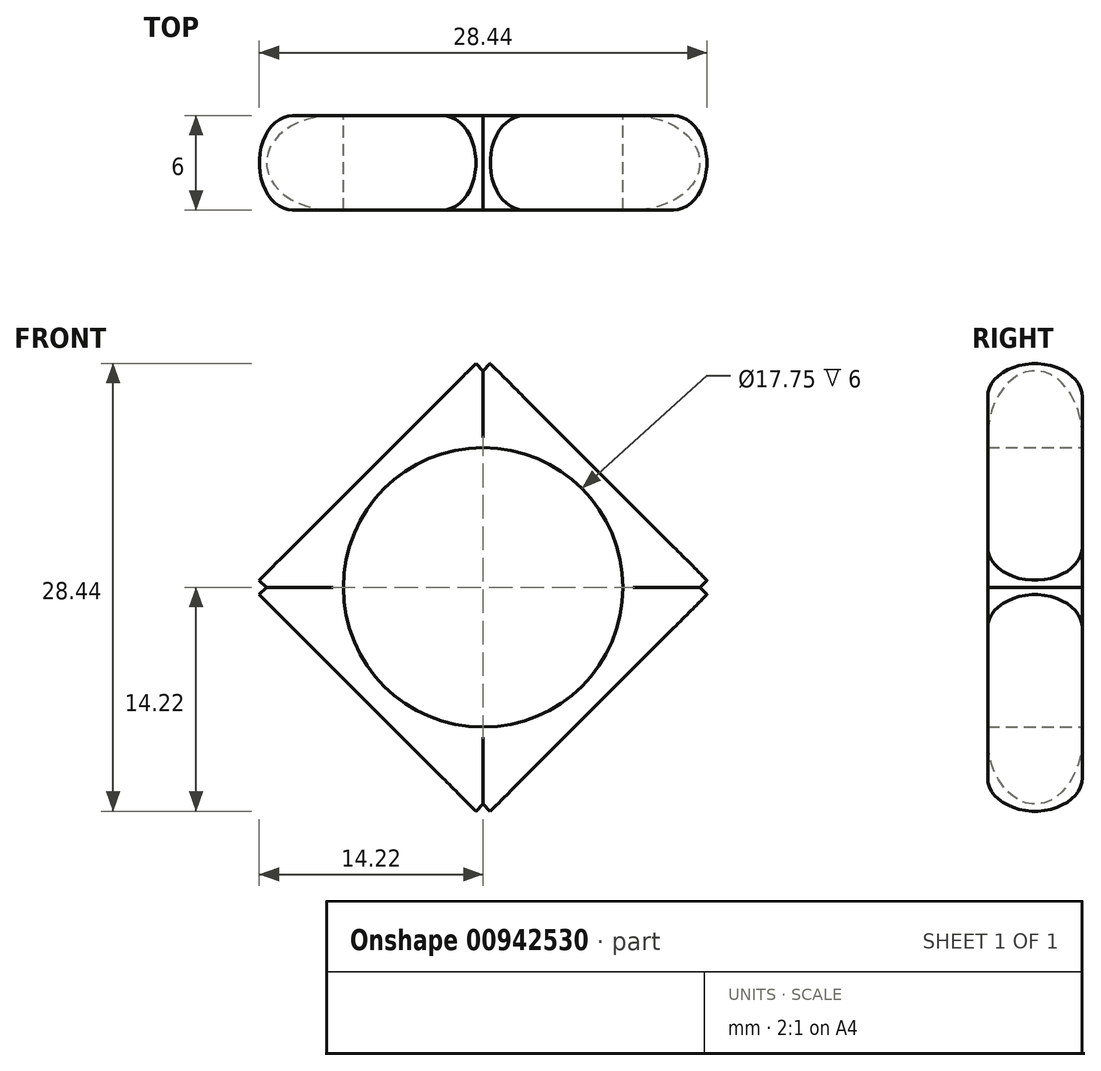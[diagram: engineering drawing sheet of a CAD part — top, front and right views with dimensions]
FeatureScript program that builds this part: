
annotation { "Feature Type Name" : "Feature", "Feature Type Description" : "" }
export const myFeature = defineFeature(function(context is Context, id is Id, definition is map)
    precondition{}
    {
        {
            var Q0;
            Q0=qCreatedBy(makeId("Front.planeOp"),FACE);
            var sketch = newSketch(context, id + "F0", { "sketchPlane" : qUnion([Q0])});
            skCircle(sketch, "E0", {"center": v(0, 0) * mm, "radius": 8.88 * mm});
            skCircle(sketch, "E1.0", {"center": v(0, 0) * mm, "radius": 10.38 * mm});
            skLineSegment(sketch, "E2", {"start": v(0, 10.37) * mm, "end": v(0, 11.88) * mm, "construction": true});
            skLineSegment(sketch, "E3", {"start": v(-14.67, 0) * mm, "end": v(0, 14.67) * mm});
            skLineSegment(sketch, "E4.MirrorCS", {"start": v(14.67, 0) * mm, "end": v(0, 14.67) * mm});
            skLineSegment(sketch, "E5.MirrorCS", {"start": v(14.67, 0) * mm, "end": v(0, -14.67) * mm});
            skLineSegment(sketch, "E6.MirrorCS", {"start": v(-14.67, 0) * mm, "end": v(0, -14.67) * mm});
            skLineSegment(sketch, "E7", {"start": v(-0.46, 14.22) * mm, "end": v(0, 13.76) * mm});
            skLineSegment(sketch, "E8", {"start": v(0, 13.76) * mm, "end": v(0.46, 14.22) * mm});
            skLineSegment(sketch, "E9.MirrorCS", {"start": v(0, -13.76) * mm, "end": v(0.46, -14.22) * mm});
            skLineSegment(sketch, "E10.MirrorCS", {"start": v(-0.46, -14.22) * mm, "end": v(0, -13.76) * mm});
            skLineSegment(sketch, "E11", {"start": v(14.22, 0.46) * mm, "end": v(13.76, 0) * mm});
            skLineSegment(sketch, "E12", {"start": v(13.76, 0) * mm, "end": v(14.22, -0.46) * mm});
            skLineSegment(sketch, "E13.MirrorCS", {"start": v(-14.22, 0.46) * mm, "end": v(-13.76, 0) * mm});
            skLineSegment(sketch, "E14.MirrorCS", {"start": v(-13.76, 0) * mm, "end": v(-14.22, -0.46) * mm});
            skPoint(sketch, "E15.orphan", {"position": v(-10.37, 0) * mm});
            skSolve(sketch);
        }
        {
            var Q0;
            {var subQ0=sQuery(id+"F0.wireOp",EDGE,"E7");Q0=makeQuery(id+"F0.imprint","IMPRINT",FACE,{"disambiguationData":[TD([[makeQuery(id+"F0.imprint","IMPRINT",EDGE,{"derivedFrom":subQ0}),-1.0]])]});}
            var Q1;
            {var subQ0=sQuery(id+"F0.wireOp",EDGE,"E13.MirrorCS");Q1=makeQuery(id+"F0.imprint","IMPRINT",FACE,{"disambiguationData":[TD([[makeQuery(id+"F0.imprint","IMPRINT",EDGE,{"derivedFrom":subQ0}),1.0]])]});}
            var Q2;
            Q2=makeQuery(id+"F0.imprint","IMPRINT",FACE,{"disambiguationData":[TD([[makeQuery(id+"F0.imprint","IMPRINT",EDGE,{"derivedFrom":sQuery(id+"F0.wireOp",EDGE,"E0")}),-1.0]])]});
            var Q3;
            {var subQ7=sQuery(id+"F0.wireOp",EDGE,"E11");Q3=makeQuery(id+"F0.imprint","IMPRINT",FACE,{"disambiguationData":[TD([[makeQuery(id+"F0.imprint","IMPRINT",EDGE,{"derivedFrom":subQ7}),-1.0]])]});}
            var Q4;
            {var subQ0=sQuery(id+"F0.wireOp",EDGE,"E9.MirrorCS");Q4=makeQuery(id+"F0.imprint","IMPRINT",FACE,{"disambiguationData":[TD([[makeQuery(id+"F0.imprint","IMPRINT",EDGE,{"derivedFrom":subQ0}),1.0]])]});}
            extrude(context, id + "F1", {"entities" : qUnion([Q0, Q1, Q2, Q3, Q4]), "depth" : 3 * mm, "offsetDistance" : 25 * mm, "hasSecondDirection" : true, "secondDirectionOppositeDirection" : true, "secondDirectionDepth" : 3 * mm});
        }
        {
            var Q0;
            Q0=makeQuery(id+"F1.opExtrude","CAP_EDGE",EDGE,{"disambiguationData":[OSD([sQuery(id+"F0.wireOp",EDGE,"E8")])],"isStart":false});
            var Q1;
            Q1=makeQuery(id+"F1.opExtrude","CAP_EDGE",EDGE,{"disambiguationData":[OSD([sQuery(id+"F0.wireOp",EDGE,"E7")])],"isStart":false});
            var Q2;
            Q2=makeQuery(id+"F1.opExtrude","CAP_EDGE",EDGE,{"disambiguationData":[OSD([sQuery(id+"F0.wireOp",EDGE,"E11")])],"isStart":false});
            var Q3;
            Q3=makeQuery(id+"F1.opExtrude","CAP_EDGE",EDGE,{"disambiguationData":[OSD([sQuery(id+"F0.wireOp",EDGE,"E12")])],"isStart":false});
            var Q4;
            Q4=makeQuery(id+"F1.opExtrude","CAP_EDGE",EDGE,{"disambiguationData":[OSD([sQuery(id+"F0.wireOp",EDGE,"E9.MirrorCS")])],"isStart":false});
            var Q5;
            Q5=makeQuery(id+"F1.opExtrude","CAP_EDGE",EDGE,{"disambiguationData":[OSD([sQuery(id+"F0.wireOp",EDGE,"E10.MirrorCS")])],"isStart":false});
            var Q6;
            Q6=makeQuery(id+"F1.opExtrude","CAP_EDGE",EDGE,{"disambiguationData":[OSD([sQuery(id+"F0.wireOp",EDGE,"E13.MirrorCS")])],"isStart":false});
            var Q7;
            Q7=makeQuery(id+"F1.opExtrude","CAP_EDGE",EDGE,{"disambiguationData":[OSD([sQuery(id+"F0.wireOp",EDGE,"E14.MirrorCS")])],"isStart":false});
            var Q8;
            Q8=makeQuery(id+"F1.opExtrude","CAP_EDGE",EDGE,{"disambiguationData":[OSD([sQuery(id+"F0.wireOp",EDGE,"E13.MirrorCS")])],"isStart":true});
            var Q9;
            Q9=makeQuery(id+"F1.opExtrude","CAP_EDGE",EDGE,{"disambiguationData":[OSD([sQuery(id+"F0.wireOp",EDGE,"E14.MirrorCS")])],"isStart":true});
            var Q10;
            Q10=makeQuery(id+"F1.opExtrude","CAP_EDGE",EDGE,{"disambiguationData":[OSD([sQuery(id+"F0.wireOp",EDGE,"E10.MirrorCS")])],"isStart":true});
            var Q11;
            Q11=makeQuery(id+"F1.opExtrude","CAP_EDGE",EDGE,{"disambiguationData":[OSD([sQuery(id+"F0.wireOp",EDGE,"E9.MirrorCS")])],"isStart":true});
            var Q12;
            Q12=makeQuery(id+"F1.opExtrude","CAP_EDGE",EDGE,{"disambiguationData":[OSD([sQuery(id+"F0.wireOp",EDGE,"E11")])],"isStart":true});
            var Q13;
            Q13=makeQuery(id+"F1.opExtrude","CAP_EDGE",EDGE,{"disambiguationData":[OSD([sQuery(id+"F0.wireOp",EDGE,"E12")])],"isStart":true});
            var Q14;
            Q14=makeQuery(id+"F1.opExtrude","CAP_EDGE",EDGE,{"disambiguationData":[OSD([sQuery(id+"F0.wireOp",EDGE,"E8")])],"isStart":true});
            var Q15;
            Q15=makeQuery(id+"F1.opExtrude","CAP_EDGE",EDGE,{"disambiguationData":[OSD([sQuery(id+"F0.wireOp",EDGE,"E7")])],"isStart":true});
            fillet(context, id + "F2", {"entities" : qUnion([Q0, Q1, Q2, Q3, Q4, Q5, Q6, Q7, Q8, Q9, Q10, Q11, Q12, Q13, Q14, Q15]), "tangentPropagation" : true, "radius" : 3 * mm, "defaultsChanged" : false, "vertexSettings" : [], "allowEdgeOverflow" : false});
        }
    });
